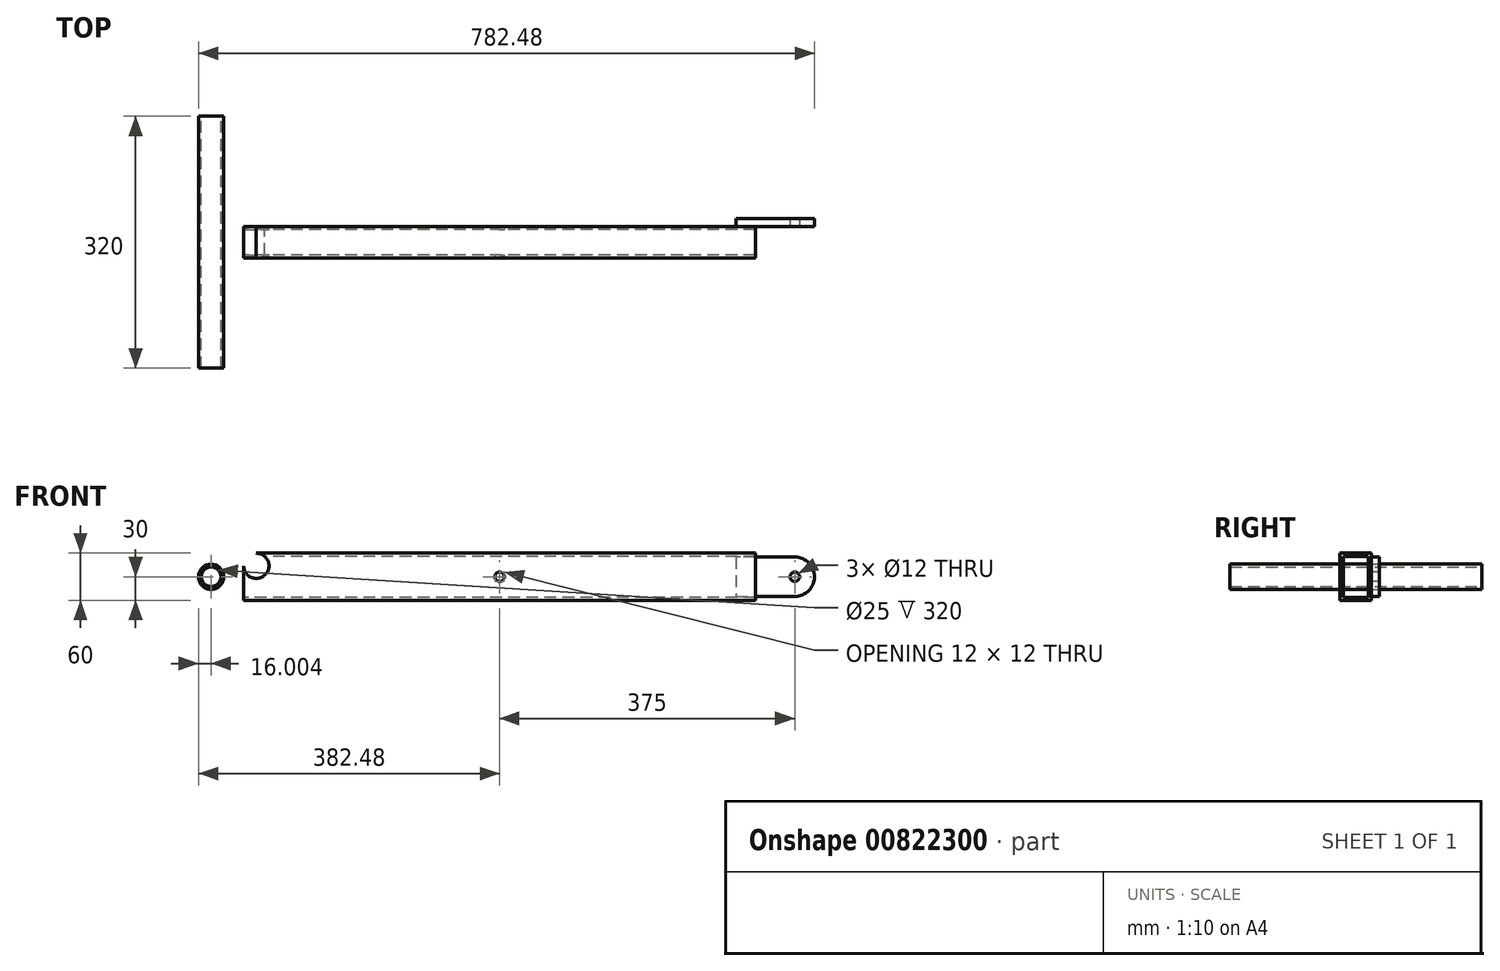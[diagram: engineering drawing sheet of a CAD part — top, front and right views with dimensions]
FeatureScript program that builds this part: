
annotation { "Feature Type Name" : "Feature", "Feature Type Description" : "" }
export const myFeature = defineFeature(function(context is Context, id is Id, definition is map)
    precondition{}
    {
        {
            var Q0;
            Q0=qCreatedBy(makeId("Right.planeOp"),FACE);
            var sketch = newSketch(context, id + "F0", { "sketchPlane" : qUnion([Q0])});
            skLineSegment(sketch, "E0.bottom", {"start": v(16, -26) * mm, "end": v(-16, -26) * mm});
            skLineSegment(sketch, "E0.top", {"start": v(16, 26) * mm, "end": v(-16, 26) * mm});
            skLineSegment(sketch, "E0.left", {"start": v(16, -26) * mm, "end": v(16, 26) * mm});
            skLineSegment(sketch, "E0.right", {"start": v(-16, -26) * mm, "end": v(-16, 26) * mm});
            skPoint(sketch, "E0.middle", {"position": v(0, 0) * mm});
            skLineSegment(sketch, "E1.bottom", {"start": v(20, -30) * mm, "end": v(-20, -30) * mm});
            skLineSegment(sketch, "E1.top", {"start": v(20, 30) * mm, "end": v(-20, 30) * mm});
            skLineSegment(sketch, "E1.left", {"start": v(20, -30) * mm, "end": v(20, 30) * mm});
            skLineSegment(sketch, "E1.right", {"start": v(-20, -30) * mm, "end": v(-20, 30) * mm});
            skSolve(sketch);
        }
        {
            var Q0;
            Q0 = qSketchRegion(id + "F0", true);
            extrude(context, id + "F1", {"entities" : qUnion([Q0]), "depth" : 650 * mm, "offsetDistance" : 25 * mm});
        }
        {
            var Q0;
            Q0=makeQuery(id+"F1.opExtrude","SWEPT_FACE",FACE,{"disambiguationData":[OSD([sQuery(id+"F0.wireOp",EDGE,"E1.left")])]});
            var sketch = newSketch(context, id + "F2", { "sketchPlane" : qUnion([Q0])});
            skLineSegment(sketch, "E2", {"start": v(-650, 0) * mm, "end": v(-625, 0) * mm});
            skLineSegment(sketch, "E3", {"start": v(-625, 0) * mm, "end": v(-625, -25) * mm});
            skLineSegment(sketch, "E4", {"start": v(-625, -25) * mm, "end": v(-700, -25) * mm});
            skLineSegment(sketch, "E5", {"start": v(-700, -25) * mm, "end": v(-700, 25) * mm});
            skLineSegment(sketch, "E6", {"start": v(-700, 25) * mm, "end": v(-625, 25) * mm});
            skLineSegment(sketch, "E7", {"start": v(-625, 25) * mm, "end": v(-625, 0) * mm});
            skCircle(sketch, "E8", {"center": v(-700, 0) * mm, "radius": 25 * mm});
            skCircle(sketch, "E9", {"center": v(-700, 0) * mm, "radius": 6 * mm});
            skSolve(sketch);
        }
        {
            var Q0;
            Q0 = qSketchRegion(id + "F2", true);
            extrude(context, id + "F3", {"entities" : qUnion([Q0]), "operationType" : NewBodyOperationType.ADD, "depth" : 10 * mm, "offsetDistance" : 25 * mm});
        }
        {
            var Q0;
            Q0=makeQuery(id+"F1.opExtrude","SWEPT_FACE",FACE,{"disambiguationData":[OSD([sQuery(id+"F0.wireOp",EDGE,"E1.left")])]});
            var sketch = newSketch(context, id + "F4", { "sketchPlane" : qUnion([Q0])});
            skLineSegment(sketch, "E10", {"start": v(0, 30) * mm, "end": v(-16, 30) * mm});
            skLineSegment(sketch, "E11", {"start": v(-16, 30) * mm, "end": v(-16, 14) * mm});
            skCircle(sketch, "E12", {"center": v(-16, 14) * mm, "radius": 16 * mm});
            skLineSegment(sketch, "E13", {"start": v(0, 30) * mm, "end": v(0, 14) * mm});
            skPoint(sketch, "E13.endSnap0", {"position": v(0, 0) * mm});
            skSolve(sketch);
        }
        {
            var Q0;
            Q0 = qSketchRegion(id + "F4", true);
            extrude(context, id + "F5", {"entities" : qUnion([Q0]), "operationType" : NewBodyOperationType.REMOVE, "oppositeDirection" : true, "depth" : 40 * mm, "offsetDistance" : 25 * mm});
        }
        {
            var Q0;
            Q0=makeQuery(id+"F1.opExtrude","SWEPT_FACE",FACE,{"disambiguationData":[OSD([sQuery(id+"F0.wireOp",EDGE,"E1.left")])]});
            var sketch = newSketch(context, id + "F6", { "sketchPlane" : qUnion([Q0])});
            skLineSegment(sketch, "E14", {"start": v(-325, -30) * mm, "end": v(-325, 0) * mm});
            skCircle(sketch, "E15", {"center": v(-325, 0) * mm, "radius": 6 * mm});
            skSolve(sketch);
        }
        {
            var Q0;
            Q0 = qSketchRegion(id + "F6", true);
            extrude(context, id + "F7", {"entities" : qUnion([Q0]), "operationType" : NewBodyOperationType.REMOVE, "oppositeDirection" : true, "depth" : 40 * mm, "offsetDistance" : 25 * mm});
        }
        {
            var Q0;
            Q0=qCreatedBy(makeId("Front.planeOp"),FACE);
            var sketch = newSketch(context, id + "F8", { "sketchPlane" : qUnion([Q0])});
            skLineSegment(sketch, "E16", {"start": v(0, 0) * mm, "end": v(-41.48, 0) * mm});
            skCircle(sketch, "E17", {"center": v(-41.48, 0) * mm, "radius": 12.5 * mm});
            skCircle(sketch, "E18", {"center": v(-41.48, 0) * mm, "radius": 16 * mm});
            skSolve(sketch);
        }
        {
            var Q0;
            Q0 = qSketchRegion(id + "F8", true);
            extrude(context, id + "F9", {"entities" : qUnion([Q0]), "depth" : 320 * mm, "offsetDistance" : 25 * mm, "symmetric" : true});
        }
    });
